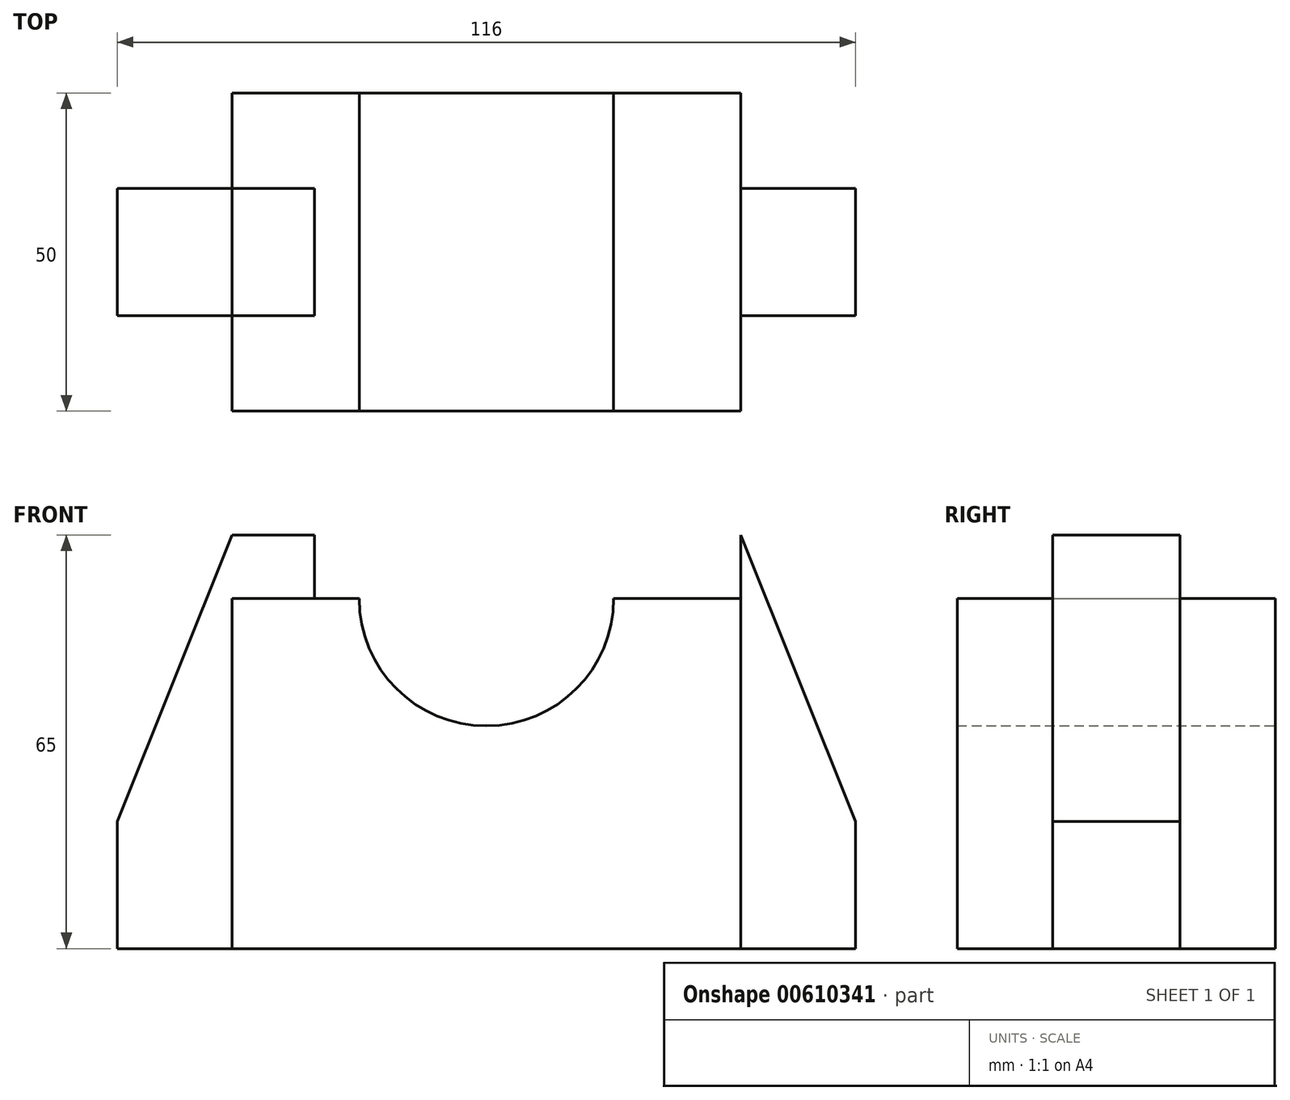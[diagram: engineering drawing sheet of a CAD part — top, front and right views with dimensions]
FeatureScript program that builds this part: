
annotation { "Feature Type Name" : "Feature", "Feature Type Description" : "" }
export const myFeature = defineFeature(function(context is Context, id is Id, definition is map)
    precondition{}
    {
        {
            var Q0;
            Q0=qCreatedBy(makeId("Front.planeOp"),FACE);
            var sketch = newSketch(context, id + "F0", { "sketchPlane" : qUnion([Q0])});
            skLineSegment(sketch, "E0.bottom", {"start": v(-40, 0) * mm, "end": v(40, 0) * mm});
            skLineSegment(sketch, "E0.top", {"start": v(-40, 55) * mm, "end": v(40, 55) * mm});
            skLineSegment(sketch, "E0.left", {"start": v(-40, 0) * mm, "end": v(-40, 55) * mm});
            skLineSegment(sketch, "E0.right", {"start": v(40, 0) * mm, "end": v(40, 55) * mm});
            skCircle(sketch, "E1", {"center": v(0, 55) * mm, "radius": 20 * mm});
            skLineSegment(sketch, "E2.bottom", {"start": v(58, 0) * mm, "end": v(40, 0) * mm});
            skLineSegment(sketch, "E2.top", {"start": v(58, 20) * mm, "end": v(40, 20) * mm});
            skLineSegment(sketch, "E2.left", {"start": v(58, 0) * mm, "end": v(58, 20) * mm});
            skLineSegment(sketch, "E2.right", {"start": v(40, 0) * mm, "end": v(40, 20) * mm});
            skLineSegment(sketch, "E3.bottom", {"start": v(40, 55) * mm, "end": v(27, 55) * mm});
            skLineSegment(sketch, "E3.top", {"start": v(40, 65) * mm, "end": v(27, 65) * mm});
            skLineSegment(sketch, "E3.left", {"start": v(40, 55) * mm, "end": v(40, 65) * mm});
            skLineSegment(sketch, "E3.right", {"start": v(27, 55) * mm, "end": v(27, 65) * mm});
            skLineSegment(sketch, "E4", {"start": v(40, 65) * mm, "end": v(58, 20) * mm});
            skLineSegment(sketch, "E5.MirrorCS", {"start": v(-27, 55) * mm, "end": v(-27, 65) * mm});
            skLineSegment(sketch, "E6.MirrorCS", {"start": v(-40, 65) * mm, "end": v(-27, 65) * mm});
            skLineSegment(sketch, "E7.MirrorCS", {"start": v(-40, 65) * mm, "end": v(-58, 20) * mm});
            skLineSegment(sketch, "E8.MirrorCS", {"start": v(-58, 0) * mm, "end": v(-58, 20) * mm});
            skLineSegment(sketch, "E9.MirrorCS", {"start": v(-58, 0) * mm, "end": v(-40, 0) * mm});
            skSolve(sketch);
        }
        {
            var Q0;
            {var subQ0=sQuery(id+"F0.wireOp",EDGE,"E1");var subQ1=sQuery(id+"F0.wireOp",EDGE,"E0.top");var subQ2=makeQuery(id+"F0.imprint","INTERSECT",VERTEX,{"disambiguationData":[OD(0.0)],"derivedFrom":[subQ1,subQ0]});Q0=makeQuery(id+"F0.imprint","IMPRINT",FACE,{"disambiguationData":[TD([[makeQuery(id+"F0.imprint","IMPRINT",EDGE,{"disambiguationData":[TD([[subQ2,-1.0]])],"derivedFrom":subQ1}),1.0]])]});}
            var Q1;
            {var subQ0=sQuery(id+"F0.wireOp",EDGE,"E1");var subQ1=sQuery(id+"F0.wireOp",EDGE,"E0.top");var subQ2=makeQuery(id+"F0.imprint","INTERSECT",VERTEX,{"disambiguationData":[OD(0.0)],"derivedFrom":[subQ1,subQ0]});Q1=makeQuery(id+"F0.imprint","IMPRINT",FACE,{"disambiguationData":[TD([[makeQuery(id+"F0.imprint","IMPRINT",EDGE,{"disambiguationData":[TD([[subQ2,-1.0]])],"derivedFrom":subQ1}),-1.0]])]});}
            var Q2;
            Q2=makeQuery(id+"F0.imprint","IMPRINT",FACE,{"disambiguationData":[TD([[makeQuery(id+"F0.imprint","IMPRINT",EDGE,{"derivedFrom":sQuery(id+"F0.wireOp",EDGE,"E0.bottom")}),1.0]])]});
            extrude(context, id + "F1", {"entities" : qUnion([Q0, Q1, Q2]), "depth" : 25 * mm, "offsetDistance" : 25 * mm, "hasSecondDirection" : true, "secondDirectionOppositeDirection" : true, "secondDirectionDepth" : 25 * mm});
        }
        {
            var Q0;
            Q0=makeQuery(id+"F1.opExtrude","CAP_FACE",FACE,{"disambiguationData":[OSD([sQuery(id+"F0.wireOp",EDGE,"E0.bottom"),sQuery(id+"F0.wireOp",EDGE,"E0.top"),sQuery(id+"F0.wireOp",EDGE,"E0.left"),sQuery(id+"F0.wireOp",EDGE,"E0.right"),sQuery(id+"F0.wireOp",EDGE,"E1")])],"isStart":false});
            var sketch = newSketch(context, id + "F2", { "sketchPlane" : qUnion([Q0])});
            skLineSegment(sketch, "E10.bottom", {"start": v(-22.97, 90.48) * mm, "end": v(22.02, 90.48) * mm});
            skLineSegment(sketch, "E10.top", {"start": v(-22.97, 65) * mm, "end": v(22.02, 65) * mm});
            skLineSegment(sketch, "E10.left", {"start": v(-22.97, 90.48) * mm, "end": v(-22.97, 65) * mm});
            skLineSegment(sketch, "E10.right", {"start": v(22.02, 90.48) * mm, "end": v(22.02, 65) * mm});
            skLineSegment(sketch, "E11.bottom", {"start": v(0, 65) * mm, "end": v(8, 65) * mm});
            skLineSegment(sketch, "E11.top", {"start": v(0, 55) * mm, "end": v(8, 55) * mm});
            skLineSegment(sketch, "E11.left", {"start": v(0, 65) * mm, "end": v(0, 55) * mm});
            skLineSegment(sketch, "E11.right", {"start": v(8, 65) * mm, "end": v(8, 55) * mm});
            skLineSegment(sketch, "E12.bottom", {"start": v(0, 65) * mm, "end": v(-8, 65) * mm});
            skLineSegment(sketch, "E12.top", {"start": v(0, 55) * mm, "end": v(-8, 55) * mm});
            skLineSegment(sketch, "E12.right", {"start": v(-8, 65) * mm, "end": v(-8, 55) * mm});
            skSolve(sketch);
        }
        {
            var Q0;
            Q0=makeQuery(id+"F2.imprint","IMPRINT",FACE,{"disambiguationData":[TD([[makeQuery(id+"F2.imprint","IMPRINT",EDGE,{"derivedFrom":sQuery(id+"F2.wireOp",EDGE,"E10.bottom")}),-1.0]])]});
            var Q1;
            {var subQ0=sQuery(id+"F2.wireOp",EDGE,"E10.top");var subQ1=makeQuery(id+"F1.opExtrude","CAP_EDGE",EDGE,{"disambiguationData":[OSD([sQuery(id+"F0.wireOp",EDGE,"E1")])],"isStart":false});var subQ2=makeQuery(id+"F2.imprint","INTERSECT",VERTEX,{"disambiguationData":[OD(0.0)],"derivedFrom":[subQ1,subQ0]});Q1=makeQuery(id+"F2.imprint","IMPRINT",FACE,{"disambiguationData":[TD([[makeQuery(id+"F2.imprint","IMPRINT",EDGE,{"disambiguationData":[TD([[subQ2,-1.0]])],"derivedFrom":subQ0}),1.0]])]});}
            var Q2;
            Q2=makeQuery(id+"F2.imprint","IMPRINT",FACE,{"disambiguationData":[TD([[makeQuery(id+"F2.imprint","IMPRINT",EDGE,{"derivedFrom":sQuery(id+"F2.wireOp",EDGE,"E11.bottom")}),-1.0]])]});
            var Q3;
            Q3=makeQuery(id+"F2.imprint","IMPRINT",FACE,{"disambiguationData":[TD([[makeQuery(id+"F2.imprint","IMPRINT",EDGE,{"derivedFrom":sQuery(id+"F2.wireOp",EDGE,"E12.bottom")}),1.0]])]});
            extrude(context, id + "F3", {"entities" : qUnion([Q0, Q1, Q2, Q3]), "operationType" : NewBodyOperationType.REMOVE, "oppositeDirection" : true, "depth" : 30 * mm, "offsetDistance" : 25 * mm});
        }
        {
            var Q0;
            {var subQ1=sQuery(id+"F0.wireOp",EDGE,"E0.left");Q0=makeQuery(id+"F0.imprint","IMPRINT",FACE,{"disambiguationData":[TD([[makeQuery(id+"F0.imprint","IMPRINT",EDGE,{"derivedFrom":subQ1}),1.0]])]});}
            var Q1;
            Q1=makeQuery(id+"F0.imprint","IMPRINT",FACE,{"disambiguationData":[TD([[makeQuery(id+"F0.imprint","IMPRINT",EDGE,{"derivedFrom":sQuery(id+"F0.wireOp",EDGE,"E0.right")}),-1.0]])]});
            var Q2;
            Q2=makeQuery(id+"F0.imprint","IMPRINT",FACE,{"disambiguationData":[TD([[makeQuery(id+"F0.imprint","IMPRINT",EDGE,{"derivedFrom":sQuery(id+"F0.wireOp",EDGE,"E3.bottom")}),-1.0]])]});
            var Q3;
            Q3=makeQuery(id+"F0.imprint","IMPRINT",FACE,{"disambiguationData":[TD([[makeQuery(id+"F0.imprint","IMPRINT",EDGE,{"derivedFrom":sQuery(id+"F0.wireOp",EDGE,"E2.bottom")}),-1.0]])]});
            extrude(context, id + "F4", {"entities" : qUnion([Q0, Q1, Q2, Q3]), "operationType" : NewBodyOperationType.ADD, "depth" : 10 * mm, "offsetDistance" : 25 * mm, "hasSecondDirection" : true, "secondDirectionOppositeDirection" : true, "secondDirectionDepth" : 10 * mm});
        }
    });
